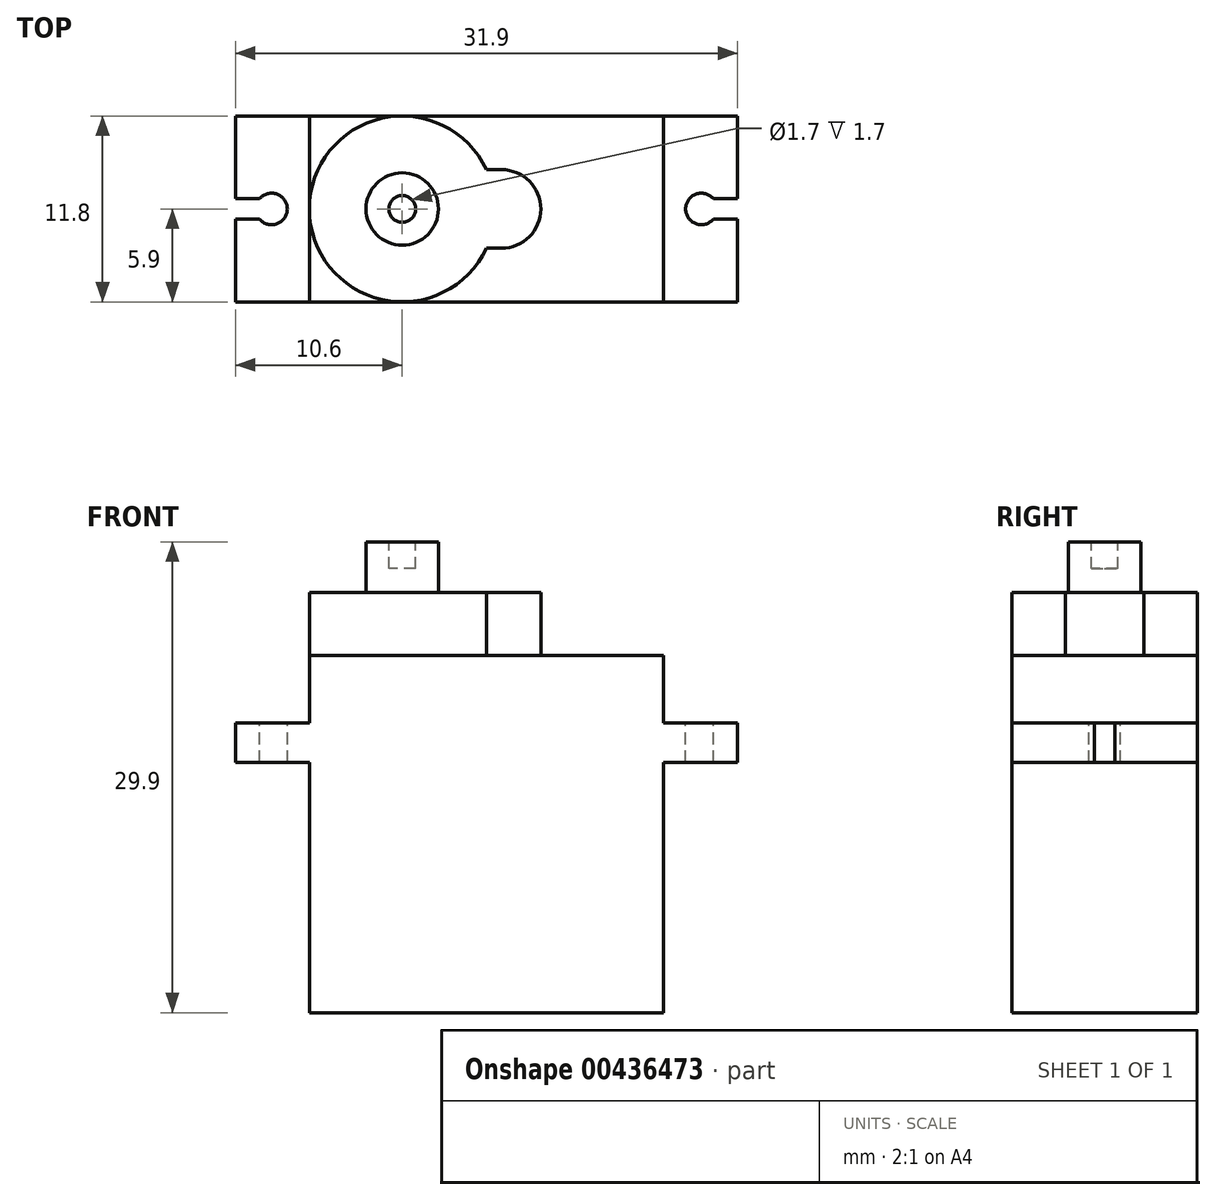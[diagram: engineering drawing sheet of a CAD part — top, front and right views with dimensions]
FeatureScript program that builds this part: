
annotation { "Feature Type Name" : "Feature", "Feature Type Description" : "" }
export const myFeature = defineFeature(function(context is Context, id is Id, definition is map)
    precondition{}
    {
        {
            var Q0;
            Q0=qCreatedBy(makeId("Front.planeOp"),FACE);
            var sketch = newSketch(context, id + "F0", { "sketchPlane" : qUnion([Q0])});
            skLineSegment(sketch, "E0.bottom", {"start": v(0, 0) * mm, "end": v(22.5, 0) * mm});
            skLineSegment(sketch, "E0.top", {"start": v(0, 22.7) * mm, "end": v(22.5, 22.7) * mm});
            skLineSegment(sketch, "E0.left", {"start": v(0, 0) * mm, "end": v(0, 15.9) * mm});
            skLineSegment(sketch, "E0.right", {"start": v(22.5, 0) * mm, "end": v(22.5, 15.9) * mm});
            skLineSegment(sketch, "E1.bottom", {"start": v(-4.7, 18.4) * mm, "end": v(0, 18.4) * mm});
            skLineSegment(sketch, "E1.top", {"start": v(-4.7, 15.9) * mm, "end": v(0, 15.9) * mm});
            skLineSegment(sketch, "E1.left", {"start": v(-4.7, 18.4) * mm, "end": v(-4.7, 15.9) * mm});
            skLineSegment(sketch, "E1.right", {"start": v(27.2, 18.4) * mm, "end": v(27.2, 15.9) * mm});
            skLineSegment(sketch, "E2.trimOffspring", {"start": v(22.5, 15.9) * mm, "end": v(27.2, 15.9) * mm});
            skLineSegment(sketch, "E3.trimOffspring", {"start": v(22.5, 18.4) * mm, "end": v(27.2, 18.4) * mm});
            skLineSegment(sketch, "E4.trimOffspring", {"start": v(0, 18.4) * mm, "end": v(0, 22.7) * mm});
            skLineSegment(sketch, "E5.trimOffspring", {"start": v(22.5, 18.4) * mm, "end": v(22.5, 22.7) * mm});
            skSolve(sketch);
        }
        {
            var Q0;
            Q0=qSketchRegion(id+"F0",true);
            extrude(context, id + "F1", {"entities" : qUnion([Q0]), "oppositeDirection" : true, "depth" : 11.8 * mm});
        }
        {
            var Q0;
            Q0=makeQuery(id+"F1.opExtrude","SWEPT_FACE",FACE,{"disambiguationData":[OSD([sQuery(id+"F0.wireOp",EDGE,"E0.top")])]});
            var sketch = newSketch(context, id + "F2", { "sketchPlane" : qUnion([Q0])});
            skArc(sketch, "E6", {"start": v(11.24, 8.4) * mm, "mid": v(0, 5.9) * mm, "end": v(11.24, 3.4) * mm});
            skLineSegment(sketch, "E7", {"start": v(5.9, 5.9) * mm, "end": v(22.5, 5.9) * mm, "construction": true});
            skLineSegment(sketch, "E8.bottom", {"start": v(11.24, 8.4) * mm, "end": v(12.2, 8.4) * mm});
            skLineSegment(sketch, "E8.top", {"start": v(11.24, 3.4) * mm, "end": v(12.2, 3.4) * mm});
            skArc(sketch, "E9", {"start": v(12.2, 3.4) * mm, "mid": v(14.7, 5.9) * mm, "end": v(12.2, 8.4) * mm});
            skPoint(sketch, "E10", {"position": v(14.7, 5.9) * mm});
            skPoint(sketch, "E11", {"position": v(4.5, 13.97) * mm});
            skSolve(sketch);
        }
        {
            var Q0;
            Q0=qSketchRegion(id+"F2",true);
            extrude(context, id + "F3", {"entities" : qUnion([Q0]), "operationType" : NewBodyOperationType.ADD, "depth" : 4 * mm});
        }
        {
            var Q0;
            Q0=makeQuery(id+"F1.opExtrude","SWEPT_FACE",FACE,{"disambiguationData":[OSD([sQuery(id+"F0.wireOp",EDGE,"E3.trimOffspring")])]});
            var sketch = newSketch(context, id + "F4", { "sketchPlane" : qUnion([Q0])});
            skPoint(sketch, "E12", {"position": v(27.2, 5.9) * mm});
            skLineSegment(sketch, "E13.bottom", {"start": v(27.2, 6.55) * mm, "end": v(25.66, 6.55) * mm});
            skLineSegment(sketch, "E13.top", {"start": v(27.2, 5.25) * mm, "end": v(25.66, 5.25) * mm});
            skLineSegment(sketch, "E13.left", {"start": v(27.2, 6.55) * mm, "end": v(27.2, 5.25) * mm});
            skArc(sketch, "E14", {"start": v(25.66, 6.55) * mm, "mid": v(23.9, 5.9) * mm, "end": v(25.66, 5.25) * mm});
            skSolve(sketch);
        }
        {
            var Q0;
            Q0=qSketchRegion(id+"F4",true);
            extrude(context, id + "F5", {"entities" : qUnion([Q0]), "operationType" : NewBodyOperationType.REMOVE, "oppositeDirection" : true, "depth" : 25 * mm});
        }
        {
            var Q0;
            Q0=makeQuery(id+"F1.opExtrude","SWEPT_FACE",FACE,{"disambiguationData":[OSD([sQuery(id+"F0.wireOp",EDGE,"E1.bottom")])]});
            var sketch = newSketch(context, id + "F6", { "sketchPlane" : qUnion([Q0])});
            skPoint(sketch, "E15", {"position": v(-4.7, 5.9) * mm});
            skLineSegment(sketch, "E16.bottom", {"start": v(-4.7, 6.55) * mm, "end": v(-3.16, 6.55) * mm});
            skLineSegment(sketch, "E16.top", {"start": v(-4.7, 5.25) * mm, "end": v(-3.16, 5.25) * mm});
            skLineSegment(sketch, "E16.left", {"start": v(-4.7, 6.55) * mm, "end": v(-4.7, 5.25) * mm});
            skArc(sketch, "E17", {"start": v(-3.16, 5.25) * mm, "mid": v(-1.4, 5.9) * mm, "end": v(-3.16, 6.55) * mm});
            skSolve(sketch);
        }
        {
            var Q0;
            Q0=qSketchRegion(id+"F6",true);
            extrude(context, id + "F7", {"entities" : qUnion([Q0]), "operationType" : NewBodyOperationType.REMOVE, "oppositeDirection" : true, "depth" : 25 * mm});
        }
        {
            var Q0;
            Q0=makeQuery(id+"F3.opExtrude","CAP_FACE",FACE,{"disambiguationData":[OSD([sQuery(id+"F2.wireOp",EDGE,"E6"),sQuery(id+"F2.wireOp",EDGE,"E8.bottom"),sQuery(id+"F2.wireOp",EDGE,"E8.top"),sQuery(id+"F2.wireOp",EDGE,"E9")])],"isStart":false});
            var sketch = newSketch(context, id + "F8", { "sketchPlane" : qUnion([Q0])});
            skCircle(sketch, "E18", {"center": v(5.9, 5.9) * mm, "radius": 2.3 * mm});
            skSolve(sketch);
        }
        {
            var Q0;
            Q0=qSketchRegion(id+"F8",true);
            extrude(context, id + "F9", {"entities" : qUnion([Q0]), "operationType" : NewBodyOperationType.ADD, "depth" : 3.2 * mm});
        }
        {
            var Q0;
            Q0=makeQuery(id+"F9.opExtrude","CAP_FACE",FACE,{"disambiguationData":[OSD([sQuery(id+"F8.wireOp",EDGE,"E18")])],"isStart":false});
            var sketch = newSketch(context, id + "F10", { "sketchPlane" : qUnion([Q0])});
            skCircle(sketch, "E19", {"center": v(5.9, 5.9) * mm, "radius": 0.85 * mm});
            skSolve(sketch);
        }
        {
            var Q0;
            Q0=qSketchRegion(id+"F10",true);
            extrude(context, id + "F11", {"entities" : qUnion([Q0]), "operationType" : NewBodyOperationType.REMOVE, "oppositeDirection" : true, "depth" : 1.7 * mm});
        }
    });
